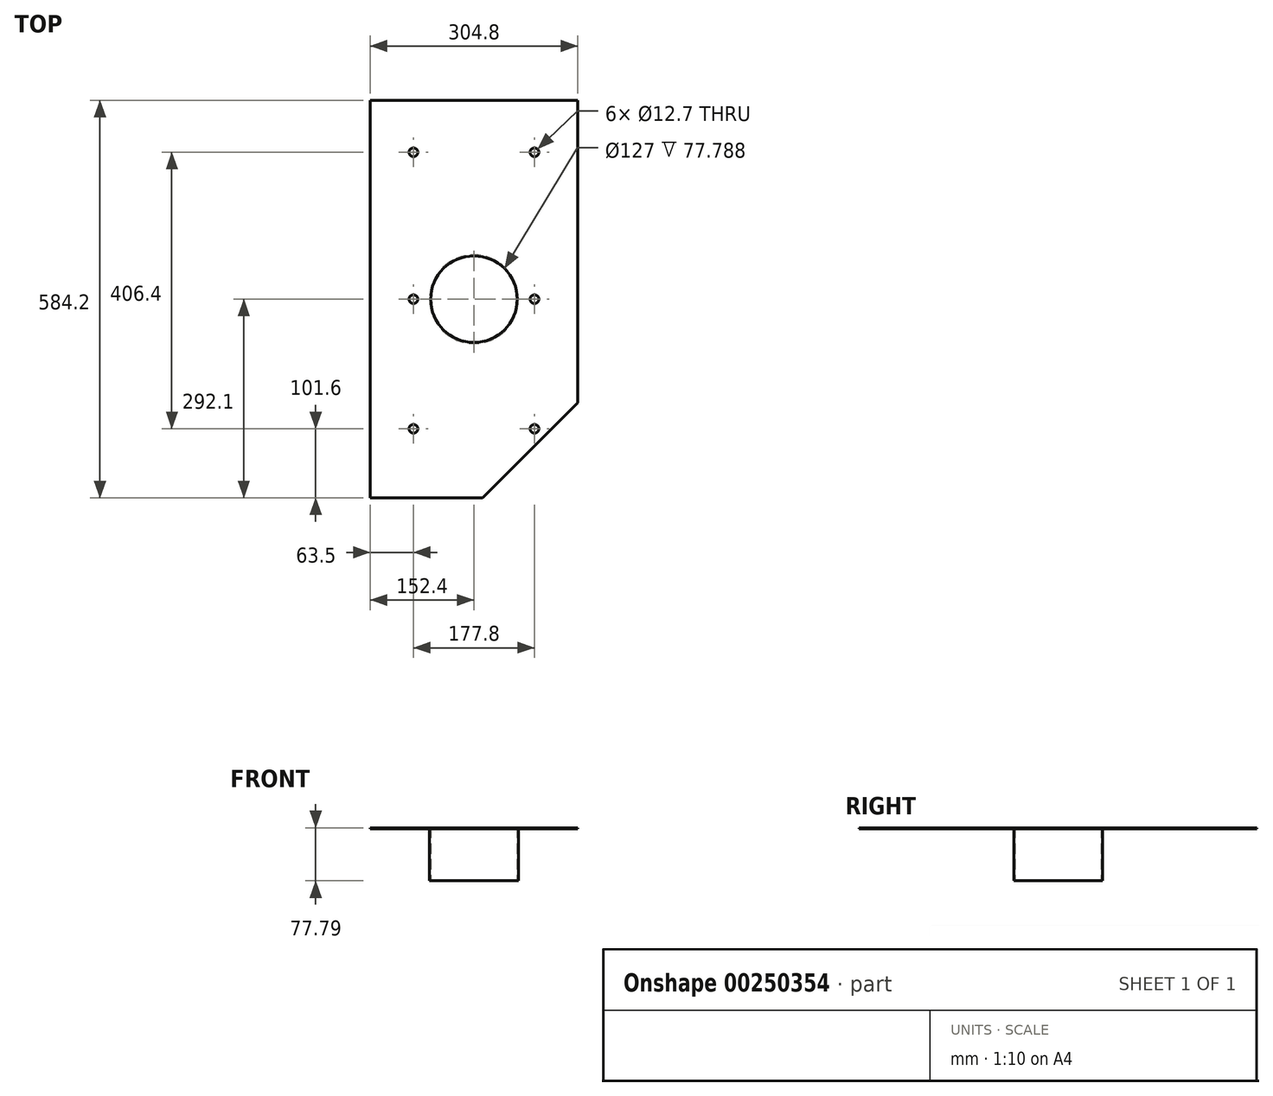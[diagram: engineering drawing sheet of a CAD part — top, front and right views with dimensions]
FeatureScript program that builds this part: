
annotation { "Feature Type Name" : "Feature", "Feature Type Description" : "" }
export const myFeature = defineFeature(function(context is Context, id is Id, definition is map)
    precondition{}
    {
        {
            var Q0;
            Q0=qCreatedBy(makeId("Top.planeOp"),FACE);
            var sketch = newSketch(context, id + "F0", { "sketchPlane" : qUnion([Q0])});
            skLineSegment(sketch, "E0.bottom", {"start": v(152.4, 292.1) * mm, "end": v(-152.4, 292.1) * mm});
            skLineSegment(sketch, "E0.top", {"start": v(12.7, -292.1) * mm, "end": v(-152.4, -292.1) * mm});
            skLineSegment(sketch, "E0.left", {"start": v(152.4, 292.1) * mm, "end": v(152.4, -152.4) * mm});
            skLineSegment(sketch, "E0.right", {"start": v(-152.4, 292.1) * mm, "end": v(-152.4, -292.1) * mm});
            skPoint(sketch, "E0.middle", {"position": v(0, 0) * mm});
            skCircle(sketch, "E1", {"center": v(0, 0) * mm, "radius": 63.5 * mm});
            skLineSegment(sketch, "E2", {"start": v(12.7, -292.1) * mm, "end": v(152.4, -152.4) * mm});
            skPoint(sketch, "E3.orphan", {"position": v(152.4, -292.1) * mm});
            skSolve(sketch);
        }
        {
            var Q0;
            Q0 = qSketchRegion(id + "F0", true);
            extrude(context, id + "F1", {"entities" : qUnion([Q0]), "depth" : 1.59 * mm});
        }
        {
            var Q0;
            Q0=makeQuery(id+"F1.opExtrude","CAP_FACE",FACE,{"disambiguationData":[OSD([sQuery(id+"F0.wireOp",EDGE,"E0.bottom"),sQuery(id+"F0.wireOp",EDGE,"E0.top"),sQuery(id+"F0.wireOp",EDGE,"E0.left"),sQuery(id+"F0.wireOp",EDGE,"E0.right"),sQuery(id+"F0.wireOp",EDGE,"E1")])],"isStart":true});
            var sketch = newSketch(context, id + "F2", { "sketchPlane" : qUnion([Q0])});
            skCircle(sketch, "E4", {"center": v(0, 0) * mm, "radius": 63.5 * mm});
            skCircle(sketch, "E5", {"center": v(0, 0) * mm, "radius": 65.09 * mm});
            skSolve(sketch);
        }
        {
            var Q0;
            Q0 = qSketchRegion(id + "F2", true);
            extrude(context, id + "F3", {"entities" : qUnion([Q0]), "operationType" : NewBodyOperationType.ADD, "depth" : 76.2 * mm});
        }
        {
            var Q0;
            Q0=makeQuery(id+"F1.opExtrude","CAP_FACE",FACE,{"disambiguationData":[OSD([sQuery(id+"F0.wireOp",EDGE,"E0.bottom"),sQuery(id+"F0.wireOp",EDGE,"E0.top"),sQuery(id+"F0.wireOp",EDGE,"E0.left"),sQuery(id+"F0.wireOp",EDGE,"E0.right"),sQuery(id+"F0.wireOp",EDGE,"E1"),sQuery(id+"F0.wireOp",EDGE,"E2")])],"isStart":false});
            var sketch = newSketch(context, id + "F4", { "sketchPlane" : qUnion([Q0])});
            skLineSegment(sketch, "E6", {"start": v(-152.4, 215.9) * mm, "end": v(152.4, 215.9) * mm});
            skLineSegment(sketch, "E7", {"start": v(-152.4, -190.5) * mm, "end": v(114.3, -190.5) * mm});
            skLineSegment(sketch, "E8", {"start": v(-88.9, 292.1) * mm, "end": v(-88.9, 209.55) * mm});
            skLineSegment(sketch, "E9", {"start": v(88.9, 292.1) * mm, "end": v(88.9, 209.55) * mm});
            skCircle(sketch, "E10", {"center": v(88.9, -190.5) * mm, "radius": 6.35 * mm});
            skCircle(sketch, "E11", {"center": v(-88.9, 215.9) * mm, "radius": 6.35 * mm});
            skCircle(sketch, "E12", {"center": v(88.9, 215.9) * mm, "radius": 6.35 * mm});
            skCircle(sketch, "E13", {"center": v(-88.9, -190.5) * mm, "radius": 6.35 * mm});
            skCircle(sketch, "E14", {"center": v(-88.9, 0) * mm, "radius": 6.35 * mm});
            skCircle(sketch, "E15", {"center": v(88.9, 0) * mm, "radius": 6.35 * mm});
            skLineSegment(sketch, "E16.trimOffspring", {"start": v(-88.9, 6.35) * mm, "end": v(-88.9, -6.35) * mm});
            skLineSegment(sketch, "E17.trimOffspring", {"start": v(88.9, 6.35) * mm, "end": v(88.9, -6.35) * mm});
            skLineSegment(sketch, "E18.trimOffspring", {"start": v(-88.9, -184.15) * mm, "end": v(-88.9, -292.1) * mm});
            skLineSegment(sketch, "E19.trimOffspring", {"start": v(88.9, -184.15) * mm, "end": v(88.9, -215.9) * mm});
            skSolve(sketch);
        }
        {
            var Q0;
            Q0 = qSketchRegion(id + "F4", true);
            extrude(context, id + "F5", {"entities" : qUnion([Q0]), "operationType" : NewBodyOperationType.REMOVE, "oppositeDirection" : true, "depth" : 25.4 * mm});
        }
    });
